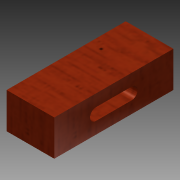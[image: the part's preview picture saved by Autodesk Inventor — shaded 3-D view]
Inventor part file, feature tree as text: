
AUTODESK INVENTOR PART (.ipt)
format: ipt  version: 2015 SP1 (Build 190203100, 203)  size: 136,192 bytes
history: native  units: in
note: dims shown in document units (in); Inventor stores cm internally (conversion verified against a paired STEP export)
features: other x3, extrude x2
ambient origin geometry x8: Origin, YZ Plane, XZ Plane, XY Plane, X Axis, Y Axis, Z Axis, Center Point
bodies: Solid1 (feature_tree)
feature tree (5):
  other  "<userpath>\Documents\2015 Offseason Chassis\West Coast Chassis Fall 2015\rivet(rv).xlsx"
  extrude  "base_extrusion"  Depth=1.0in
  extrude  "tensioner"  Depth=2.5in
  other  "tensioner_wood_block_base_sketch"
  other  "tensioner_sketch"
